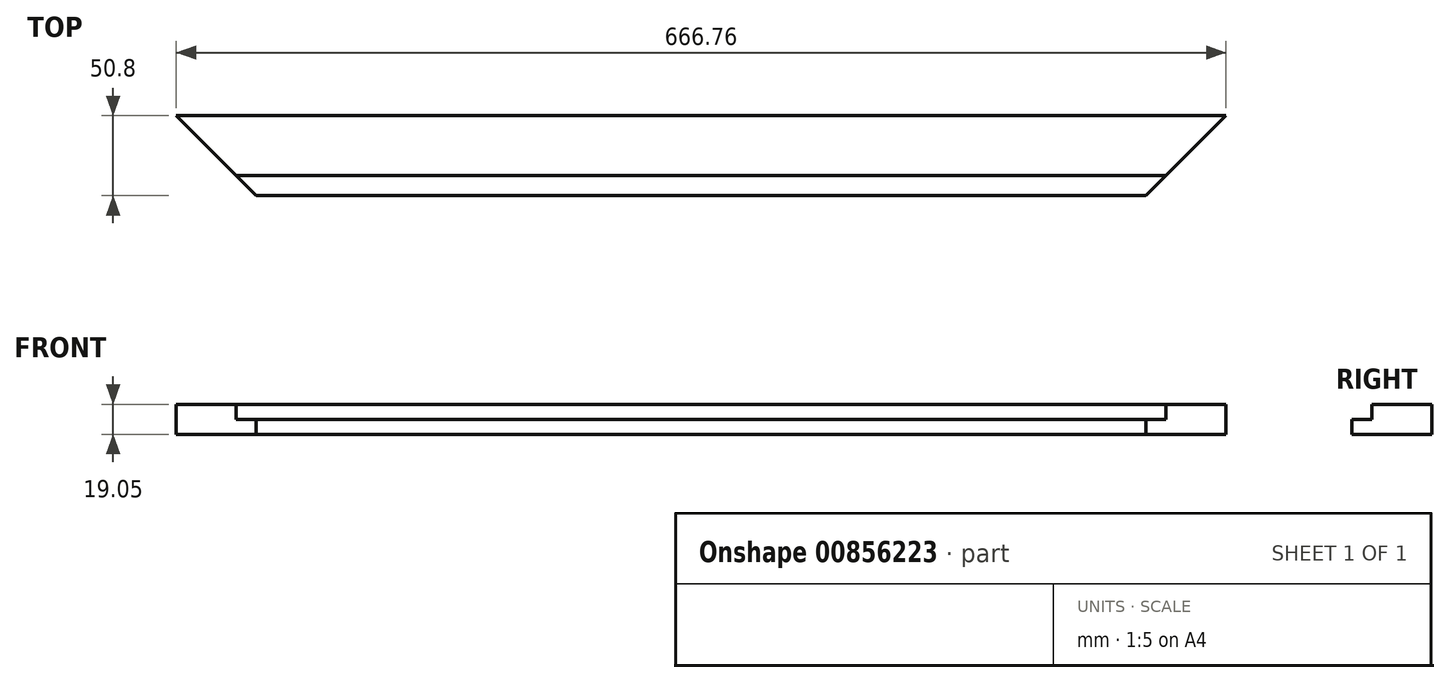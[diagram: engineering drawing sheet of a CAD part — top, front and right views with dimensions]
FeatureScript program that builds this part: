
annotation { "Feature Type Name" : "Feature", "Feature Type Description" : "" }
export const myFeature = defineFeature(function(context is Context, id is Id, definition is map)
    precondition{}
    {
        {
            var Q0;
            Q0=qCreatedBy(makeId("Top.planeOp"),FACE);
            var sketch = newSketch(context, id + "F0", { "sketchPlane" : qUnion([Q0])});
            skLineSegment(sketch, "E0.bottom", {"start": v(333.38, 25.4) * mm, "end": v(-333.38, 25.4) * mm});
            skLineSegment(sketch, "E0.top", {"start": v(333.38, -25.4) * mm, "end": v(-333.38, -25.4) * mm});
            skLineSegment(sketch, "E0.left", {"start": v(333.38, 25.4) * mm, "end": v(333.38, -25.4) * mm});
            skLineSegment(sketch, "E0.right", {"start": v(-333.38, 25.4) * mm, "end": v(-333.38, -25.4) * mm});
            skPoint(sketch, "E0.middle", {"position": v(0, 0) * mm});
            skSolve(sketch);
        }
        {
            var Q0;
            Q0 = qSketchRegion(id + "F0", true);
            extrude(context, id + "F1", {"entities" : qUnion([Q0]), "depth" : 19.05 * mm, "offsetDistance" : 25.4 * mm});
        }
        {
            var Q0;
            Q0=makeQuery(id+"F1.opExtrude","SWEPT_EDGE",EDGE,{"disambiguationData":[OSD([sQuery(id+"F0.wireOp",EDGE,"E0.top"),sQuery(id+"F0.wireOp",EDGE,"E0.left")])]});
            var Q1;
            Q1=makeQuery(id+"F1.opExtrude","SWEPT_EDGE",EDGE,{"disambiguationData":[OSD([sQuery(id+"F0.wireOp",EDGE,"E0.top"),sQuery(id+"F0.wireOp",EDGE,"E0.right")])]});
            chamfer(context, id + "F2", {"entities" : qUnion([Q0, Q1]), "width" : 50.8 * mm, "tangentPropagation" : true});
        }
        {
            var Q0;
            Q0=makeQuery(id+"F1.opExtrude","CAP_FACE",FACE,{"disambiguationData":[OSD([sQuery(id+"F0.wireOp",EDGE,"E0.bottom"),sQuery(id+"F0.wireOp",EDGE,"E0.top"),sQuery(id+"F0.wireOp",EDGE,"E0.left"),sQuery(id+"F0.wireOp",EDGE,"E0.right")])],"isStart":false});
            var sketch = newSketch(context, id + "F3", { "sketchPlane" : qUnion([Q0])});
            skLineSegment(sketch, "E1.0", {"start": v(282.57, -25.4) * mm, "end": v(-282.57, -25.4) * mm});
            skLineSegment(sketch, "E2.0", {"start": v(-295.27, -12.7) * mm, "end": v(-282.57, -25.4) * mm});
            skLineSegment(sketch, "E3.0", {"start": v(282.58, -25.4) * mm, "end": v(295.28, -12.7) * mm});
            skPoint(sketch, "E4.orphan", {"position": v(357.98, 0) * mm});
            skLineSegment(sketch, "E5", {"start": v(-295.27, -12.7) * mm, "end": v(295.28, -12.7) * mm});
            skPoint(sketch, "E6.orphan", {"position": v(-333.38, 25.4) * mm});
            skPoint(sketch, "E7.orphan", {"position": v(333.38, 25.4) * mm});
            skSolve(sketch);
        }
        {
            var Q0;
            Q0 = qSketchRegion(id + "F3", true);
            extrude(context, id + "F4", {"entities" : qUnion([Q0]), "operationType" : NewBodyOperationType.REMOVE, "oppositeDirection" : true, "depth" : 9.52 * mm, "offsetDistance" : 25.4 * mm});
        }
    });
